# Revit family: Mixer-Bath Shower-Dorf Epic Bloc Progressive1
name_source: partatom
category: Plumbing Fixtures
revit_build: Autodesk Revit 2014 (Build: 20140709_2115(x64)
units: mm (PartAtom-declared; Revit-internal decimal feet)

## types (6) — shared parameters
Assembly Code = D2020300
CW Connection = Yes
CWFU = 3
Connector Radius = 10 mm  [stored 0.0328084 ft]
Default Elevation = 1000 mm  [stored 3.28084 ft]
HW Connection = Yes
HWFU = 3
Height_ANZRS = 70 mm  [stored 0.229659 ft]
Length_ANZRS = 70 mm  [stored 0.229659 ft]
Manufacturer = GWA Bathrooms & Kitchens
ModifiedIssue_ANZRS = 20161103.01 $
URL = http://specify.caroma.com.au
Vent Connection = No
Waste Connection = No
Width_ANZRS = 36 mm  [stored 0.11811 ft]
zero-valued in all types: Cost

## per-type parameters (varying)
| type | Handle | Material_ANZRS | Model | Type Comments |
| Chrome | Metal-Chrome-Caroma | Metal-Chrome-Caroma | 6556.04 | Dorf Epic Bloc Progressive Wall Mixer - Chrome |
| Black | Metal-Brass-Powdercoated-Matte Black | Metal-Brass-Powdercoated-Matte Black | 6556.90 | Dorf Epic Bloc Progressive Wall Mixer - Black |
| Chrome with Black Handle | Metal-Brass-Powdercoated-Matte Black | Metal-Chrome-Caroma | 6557.04 | Dorf Epic Bloc Progressive Wall Mixer - Chrome with Black Handle |
| Black with Copper Handle | Metal-Copper-Satin | Metal-Brass-Powdercoated-Matte Black | 6558.90 | Dorf Epic Bloc Progressive Wall Mixer - Black with Copper Handle |
| Black with Gold Handle | Metal-Gold-Fine | Metal-Brass-Powdercoated-Matte Black | 6559.90 | Dorf Epic Bloc Progressive Wall Mixer - Black with Gold Handle |
| Black with Rose Gold Handle | Metal-Gold-Rose | Metal-Brass-Powdercoated-Matte Black | 6557.90 | Dorf Epic Bloc Progressive Wall Mixer - Black with Rose Gold Handle |

note: [stored X ft] marks values corroborated as IEEE doubles in the binary element streams (Revit-internal decimal feet)

## geometry (parser evidence)
native form markers: Blend x8, Sweep x1
no freeform markers — native parametric forms only
